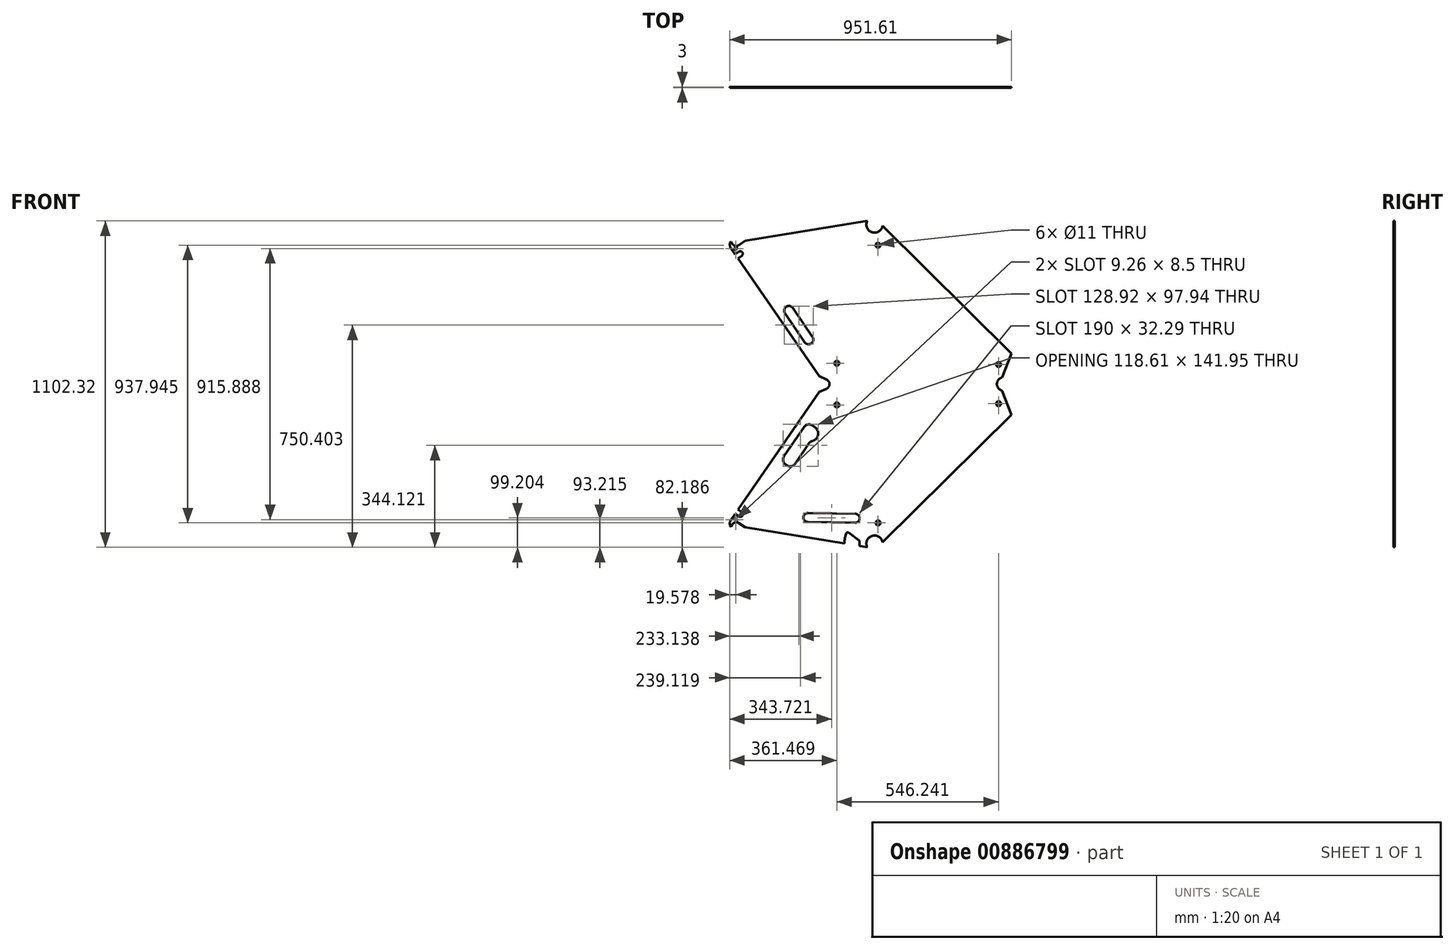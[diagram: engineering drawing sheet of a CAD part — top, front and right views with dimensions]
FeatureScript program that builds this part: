
annotation { "Feature Type Name" : "Feature", "Feature Type Description" : "" }
export const myFeature = defineFeature(function(context is Context, id is Id, definition is map)
    precondition{}
    {
        {
            var Q0;
            Q0=qCreatedBy(makeId("Front.planeOp"),FACE);
            var sketch = newSketch(context, id + "F0", { "sketchPlane" : qUnion([Q0])});
            skCircle(sketch, "E0", {"center": v(1053.9, -134.2) * mm, "radius": 17 * mm, "construction": true});
            skCircle(sketch, "E1", {"center": v(1053.9, -134.2) * mm, "radius": 21.5 * mm, "construction": true});
            skLineSegment(sketch, "E2", {"start": v(622.48, -20.32) * mm, "end": v(871.92, 345.36) * mm, "construction": true});
            skLineSegment(sketch, "E3", {"start": v(615.02, -14.4) * mm, "end": v(879.24, 372.95) * mm, "construction": true});
            skLineSegment(sketch, "E4", {"start": v(1053.9, -134.22) * mm, "end": v(865.03, 414.2) * mm, "construction": true});
            skLineSegment(sketch, "E5", {"start": v(1034.15, -125.7) * mm, "end": v(850, 409.01) * mm, "construction": true});
            skLineSegment(sketch, "E6", {"start": v(861.66, 381.3) * mm, "end": v(851.9, 409.67) * mm, "construction": true});
            skLineSegment(sketch, "E7", {"start": v(1064.21, -115.34) * mm, "end": v(880.07, 419.37) * mm, "construction": true});
            skLineSegment(sketch, "E8", {"start": v(1053.9, -134.2) * mm, "end": v(645.8, -73.78) * mm, "construction": true});
            skLineSegment(sketch, "E9", {"start": v(743.09, -99.4) * mm, "end": v(644.17, -84.76) * mm, "construction": true});
            skLineSegment(sketch, "E10", {"start": v(746.34, -77.44) * mm, "end": v(647.42, -62.8) * mm, "construction": true});
            skLineSegment(sketch, "E11", {"start": v(1035.36, -145.1) * mm, "end": v(841.66, -116.43) * mm, "construction": true});
            skLineSegment(sketch, "E12", {"start": v(1039.32, -118.4) * mm, "end": v(845.61, -89.72) * mm, "construction": true});
            skLineSegment(sketch, "E13", {"start": v(966.15, -134.86) * mm, "end": v(995.58, -139.21) * mm, "construction": true});
            skLineSegment(sketch, "E14", {"start": v(960.23, -139.03) * mm, "end": v(994.85, -144.16) * mm, "construction": true});
            skLineSegment(sketch, "E15", {"start": v(963.6, -143.58) * mm, "end": v(964.04, -140.6) * mm, "construction": true});
            skArc(sketch, "E16", {"start": v(959.64, -143) * mm, "mid": v(959.83, -143.73) * mm, "end": v(960.48, -144.13) * mm, "construction": true});
            skLineSegment(sketch, "E17", {"start": v(960.48, -144.13) * mm, "end": v(962.46, -144.42) * mm, "construction": true});
            skArc(sketch, "E18", {"start": v(962.46, -144.42) * mm, "mid": v(963.2, -144.23) * mm, "end": v(963.6, -143.58) * mm, "construction": true});
            skLineSegment(sketch, "E19", {"start": v(965.3, -133.72) * mm, "end": v(967.21, -120.86) * mm, "construction": true});
            skLineSegment(sketch, "E20", {"start": v(963, -120.24) * mm, "end": v(959.64, -143) * mm, "construction": true});
            skLineSegment(sketch, "E21", {"start": v(962.42, -124.2) * mm, "end": v(966.63, -124.82) * mm, "construction": true});
            skArc(sketch, "E22", {"start": v(965.17, -139.77) * mm, "mid": v(964.43, -139.95) * mm, "end": v(964.04, -140.6) * mm, "construction": true});
            skLineSegment(sketch, "E23", {"start": v(961.7, -129.14) * mm, "end": v(965.9, -129.76) * mm, "construction": true});
            skLineSegment(sketch, "E24", {"start": v(960.08, -126.38) * mm, "end": v(968.24, -127.58) * mm, "construction": true});
            skLineSegment(sketch, "E25", {"start": v(974.82, -141.2) * mm, "end": v(975.55, -136.25) * mm, "construction": true});
            skArc(sketch, "E26", {"start": v(965.3, -133.72) * mm, "mid": v(965.5, -134.46) * mm, "end": v(966.15, -134.86) * mm, "construction": true});
            skLineSegment(sketch, "E27", {"start": v(964.14, -119.4) * mm, "end": v(966.37, -119.73) * mm, "construction": true});
            skArc(sketch, "E28", {"start": v(964.14, -119.4) * mm, "mid": v(963.4, -119.58) * mm, "end": v(963, -120.24) * mm, "construction": true});
            skArc(sketch, "E29", {"start": v(967.21, -120.86) * mm, "mid": v(967.03, -120.12) * mm, "end": v(966.37, -119.73) * mm, "construction": true});
            skLineSegment(sketch, "E30", {"start": v(995.58, -139.21) * mm, "end": v(999.8, -144.9) * mm, "construction": true});
            skLineSegment(sketch, "E31", {"start": v(979.72, -143.94) * mm, "end": v(981.04, -135.04) * mm, "construction": true});
            skArc(sketch, "E32", {"start": v(995.7, -145.3) * mm, "mid": v(995.5, -144.55) * mm, "end": v(994.85, -144.16) * mm, "construction": true});
            skArc(sketch, "E33", {"start": v(995.25, -148.26) * mm, "mid": v(995.44, -149) * mm, "end": v(996.1, -149.4) * mm, "construction": true});
            skArc(sketch, "E34", {"start": v(998.07, -149.7) * mm, "mid": v(998.82, -149.5) * mm, "end": v(999.2, -148.85) * mm, "construction": true});
            skLineSegment(sketch, "E35", {"start": v(996.1, -149.4) * mm, "end": v(998.07, -149.7) * mm, "construction": true});
            skLineSegment(sketch, "E36", {"start": v(999.2, -148.85) * mm, "end": v(999.8, -144.9) * mm, "construction": true});
            skLineSegment(sketch, "E37", {"start": v(995.25, -148.26) * mm, "end": v(995.7, -145.3) * mm, "construction": true});
            skLineSegment(sketch, "E38", {"start": v(985.2, -142.73) * mm, "end": v(985.94, -137.79) * mm, "construction": true});
            skLineSegment(sketch, "E39", {"start": v(995.47, -146.78) * mm, "end": v(993.6, -159.38) * mm, "construction": true});
            skLineSegment(sketch, "E40", {"start": v(850, 409.01) * mm, "end": v(880.07, 419.37) * mm, "construction": true});
            skLineSegment(sketch, "E41", {"start": v(859.77, 380.65) * mm, "end": v(861.66, 381.3) * mm, "construction": true});
            skLineSegment(sketch, "E42", {"start": v(1053.9, -134.22) * mm, "end": v(1520.05, 326.73) * mm, "construction": true});
            skLineSegment(sketch, "E43", {"start": v(1081.03, -129.75) * mm, "end": v(1510.36, 294.78) * mm, "construction": true});
            skLineSegment(sketch, "E44", {"start": v(1060.7, -105.14) * mm, "end": v(1497.91, 327.2) * mm, "construction": true});
            skLineSegment(sketch, "E45", {"start": v(879.24, 372.95) * mm, "end": v(1402.67, 372.95) * mm, "construction": true});
            skLineSegment(sketch, "E46", {"start": v(901.53, 357.05) * mm, "end": v(1486.45, 357.05) * mm, "construction": true});
            skLineSegment(sketch, "E47", {"start": v(890.58, 388.85) * mm, "end": v(1474.25, 388.85) * mm, "construction": true});
            skArc(sketch, "E48", {"start": v(1486.5, 356.93) * mm, "mid": v(1487.54, 375.64) * mm, "end": v(1474.25, 388.85) * mm, "construction": true});
            skArc(sketch, "E49", {"start": v(890.58, 388.85) * mm, "mid": v(888.92, 370.5) * mm, "end": v(901.53, 357.05) * mm, "construction": true});
            skArc(sketch, "E50", {"start": v(1510.36, 294.78) * mm, "mid": v(1511.76, 313.92) * mm, "end": v(1497.91, 327.2) * mm, "construction": true});
            skArc(sketch, "E51", {"start": v(919.09, -223.5) * mm, "mid": v(918.34, -223.31) * mm, "end": v(917.6, -223.13) * mm, "construction": true});
            skFitSpline(sketch, "E52", {"points": [v(871.92, 345.36) * mm, v(875.7, 355.52) * mm, v(881.2, 370.3) * mm, v(868.26, 368.37) * mm, v(864.2, 367.77) * mm], "construction": true});
            skLineSegment(sketch, "E53", {"start": v(587.46, -71.43) * mm, "end": v(605.08, -83.05) * mm, "construction": true});
            skLineSegment(sketch, "E54", {"start": v(584.15, -63.19) * mm, "end": v(613.37, -82.46) * mm, "construction": true});
            skLineSegment(sketch, "E55", {"start": v(607.46, -8.63) * mm, "end": v(607.4, -8.7) * mm, "construction": true});
            skLineSegment(sketch, "E56", {"start": v(644.18, -84.66) * mm, "end": v(644.29, -83.94) * mm, "construction": true});
            skLineSegment(sketch, "E57", {"start": v(644.18, -84.66) * mm, "end": v(622.66, -81.47) * mm, "construction": true});
            skArc(sketch, "E58", {"start": v(644.63, -83.68) * mm, "mid": v(644.4, -83.74) * mm, "end": v(644.29, -83.94) * mm, "construction": true});
            skLineSegment(sketch, "E59", {"start": v(644.18, -84.66) * mm, "end": v(644.19, -84.63) * mm, "construction": true});
            skArc(sketch, "E60", {"start": v(617.78, -52.64) * mm, "mid": v(628.06, -58.54) * mm, "end": v(639.47, -61.73) * mm, "construction": true});
            skLineSegment(sketch, "E61", {"start": v(670.48, -77.43) * mm, "end": v(577.33, -63.64) * mm, "construction": true});
            skLineSegment(sketch, "E62", {"start": v(647.4, -62.9) * mm, "end": v(639.47, -61.73) * mm, "construction": true});
            skArc(sketch, "E63", {"start": v(647.3, -63.56) * mm, "mid": v(647.36, -63.78) * mm, "end": v(647.56, -63.9) * mm, "construction": true});
            skLineSegment(sketch, "E64", {"start": v(647.3, -63.56) * mm, "end": v(647.4, -62.9) * mm, "construction": true});
            skArc(sketch, "E65", {"start": v(614, -32.51) * mm, "mid": v(611.92, -43.32) * mm, "end": v(617.78, -52.64) * mm, "construction": true});
            skLineSegment(sketch, "E66", {"start": v(614, -32.51) * mm, "end": v(622.56, -20.17) * mm, "construction": true});
            skLineSegment(sketch, "E67", {"start": v(576.98, -64.11) * mm, "end": v(629.71, 4.8) * mm, "construction": true});
            skArc(sketch, "E68", {"start": v(572.75, -54.03) * mm, "mid": v(569.56, -71.65) * mm, "end": v(582.02, -84.5) * mm, "construction": true});
            skLineSegment(sketch, "E69", {"start": v(607.46, -8.63) * mm, "end": v(608.42, -9.36) * mm, "construction": true});
            skArc(sketch, "E70", {"start": v(621.55, -19.02) * mm, "mid": v(621.5, -19.24) * mm, "end": v(621.6, -19.44) * mm, "construction": true});
            skLineSegment(sketch, "E71", {"start": v(621.6, -19.44) * mm, "end": v(622.56, -20.17) * mm, "construction": true});
            skArc(sketch, "E72", {"start": v(608.42, -9.36) * mm, "mid": v(608.64, -9.42) * mm, "end": v(608.84, -9.3) * mm, "construction": true});
            skLineSegment(sketch, "E73", {"start": v(608.42, -9.36) * mm, "end": v(607.46, -8.63) * mm, "construction": true});
            skLineSegment(sketch, "E74", {"start": v(619.71, -24.29) * mm, "end": v(604.42, -12.6) * mm, "construction": true});
            skCircle(sketch, "E75", {"center": v(600.85, -74.2) * mm, "radius": 5 * mm, "construction": true});
            skLineSegment(sketch, "E76", {"start": v(621.6, -19.44) * mm, "end": v(608.42, -9.36) * mm, "construction": true});
            skLineSegment(sketch, "E77", {"start": v(841.66, -116.43) * mm, "end": v(743.09, -99.4) * mm, "construction": true});
            skLineSegment(sketch, "E78", {"start": v(746.34, -77.44) * mm, "end": v(845.61, -89.72) * mm, "construction": true});
            skEllipse(sketch, "E79", {"center": v(843.64, -103.07) * mm, "majorRadius": 13.5 * mm, "minorRadius": 8.5 * mm, "majorAxis": v(-0.15, -0.99), "construction": true});
            skCircle(sketch, "E80", {"center": v(795.03, 249.5) * mm, "radius": 9.5 * mm, "construction": true});
            skLineSegment(sketch, "E81", {"start": v(796.02, 244.3) * mm, "end": v(795.95, 244.64) * mm, "construction": true});
            skLineSegment(sketch, "E82", {"start": v(796.02, 244.3) * mm, "end": v(789.82, 248.52) * mm, "construction": true});
            skLineSegment(sketch, "E83", {"start": v(784, 242.2) * mm, "end": v(792.26, 236.56) * mm, "construction": true});
            skLineSegment(sketch, "E84", {"start": v(792.26, 236.56) * mm, "end": v(793.8, 238.84) * mm, "construction": true});
            skLineSegment(sketch, "E85", {"start": v(791.91, 236.5) * mm, "end": v(792.26, 236.56) * mm, "construction": true});
            skLineSegment(sketch, "E86", {"start": v(795.95, 244.64) * mm, "end": v(790.17, 248.58) * mm, "construction": true});
            skLineSegment(sketch, "E87", {"start": v(791.91, 236.5) * mm, "end": v(784.06, 241.85) * mm, "construction": true});
            skLineSegment(sketch, "E88", {"start": v(789.96, 238.43) * mm, "end": v(794.75, 245.46) * mm, "construction": true});
            skLineSegment(sketch, "E89", {"start": v(790.2, 238) * mm, "end": v(795.12, 245.2) * mm, "construction": true});
            skLineSegment(sketch, "E90", {"start": v(793.8, 238.84) * mm, "end": v(785.55, 244.47) * mm, "construction": true});
            skLineSegment(sketch, "E91", {"start": v(792.78, 239.54) * mm, "end": v(796.02, 244.3) * mm, "construction": true});
            skArc(sketch, "E92", {"start": v(962.06, -126.67) * mm, "mid": v(930.44, 82.62) * mm, "end": v(787.99, 239.18) * mm, "construction": true});
            skLineSegment(sketch, "E93", {"start": v(702.12, -93.34) * mm, "end": v(670.46, -88.65) * mm, "construction": true});
            skCircle(sketch, "E94", {"center": v(1053.9, -134.2) * mm, "radius": 94.9 * mm, "construction": true});
            skCircle(sketch, "E95", {"center": v(600.85, -74.2) * mm, "radius": 41.4 * mm, "construction": true});
            skLineSegment(sketch, "E96", {"start": v(1055.81, -39.3) * mm, "end": v(601.44, -32.8) * mm, "construction": true});
            skLineSegment(sketch, "E97", {"start": v(1469.36, 401.56) * mm, "end": v(1507.64, 416.26) * mm, "construction": true});
            skLineSegment(sketch, "E98", {"start": v(1507.64, 416.26) * mm, "end": v(1552.44, 299.56) * mm, "construction": true});
            skLineSegment(sketch, "E99", {"start": v(1552.44, 299.56) * mm, "end": v(1514.16, 284.87) * mm, "construction": true});
            skLineSegment(sketch, "E100", {"start": v(1514.16, 284.87) * mm, "end": v(1469.36, 401.56) * mm, "construction": true});
            skLineSegment(sketch, "E101", {"start": v(1516.78, 301.13) * mm, "end": v(1081.03, -129.75) * mm});
            skLineSegment(sketch, "E102", {"start": v(572.75, -54.03) * mm, "end": v(878.77, 388.85) * mm, "construction": true});
            skArc(sketch, "E103", {"start": v(1081.03, -129.75) * mm, "mid": v(1045.48, -108.05) * mm, "end": v(1029.25, -146.41) * mm});
            skLineSegment(sketch, "E104.trimOffspring", {"start": v(1029.25, -146.41) * mm, "end": v(617.52, -79.2) * mm});
            skCircle(sketch, "E105", {"center": v(926.64, 334.5) * mm, "radius": 4 * mm, "construction": true});
            skCircle(sketch, "E106", {"center": v(1472.88, 338.55) * mm, "radius": 4 * mm, "construction": true});
            skCircle(sketch, "E107", {"center": v(1065.9, -64.22) * mm, "radius": 4 * mm, "construction": true});
            skLineSegment(sketch, "E108", {"start": v(1053.9, -134.22) * mm, "end": v(1237.28, -134.22) * mm, "construction": true});
            skLineSegment(sketch, "E109", {"start": v(1053.9, -134.22) * mm, "end": v(1053.9, 23.55) * mm, "construction": true});
            skCircle(sketch, "E110", {"center": v(866.64, 414.5) * mm, "radius": 25 * mm, "construction": true});
            skCircle(sketch, "E111", {"center": v(1489.1, 401.54) * mm, "radius": 28.6 * mm, "construction": true});
            skLineSegment(sketch, "E112", {"start": v(1516.78, 301.13) * mm, "end": v(1482.36, 388.85) * mm});
            skLineSegment(sketch, "E113.trimOffspring", {"start": v(875.12, 388.85) * mm, "end": v(1482.36, 388.85) * mm});
            skCircle(sketch, "E114", {"center": v(600.85, -74.2) * mm, "radius": 312.5 * mm, "construction": true});
            skLineSegment(sketch, "E115.0", {"start": v(568.9, -54.33) * mm, "end": v(583.1, -33.76) * mm});
            skArc(sketch, "E116", {"start": v(568.9, -54.33) * mm, "mid": v(565.18, -65.8) * mm, "end": v(568.38, -77.42) * mm});
            skLineSegment(sketch, "E117.trimOffspring", {"start": v(601.35, -7.36) * mm, "end": v(875.12, 388.85) * mm});
            skArc(sketch, "E118", {"start": v(594.2, -30.39) * mm, "mid": v(610.2, -27.47) * mm, "end": v(607.28, -11.47) * mm, "construction": true});
            skLineSegment(sketch, "E119", {"start": v(600.85, -74.2) * mm, "end": v(600.85, 11.26) * mm, "construction": true});
            skLineSegment(sketch, "E120", {"start": v(607.28, -11.47) * mm, "end": v(601.35, -7.36) * mm, "construction": true});
            skLineSegment(sketch, "E121", {"start": v(601.35, -7.36) * mm, "end": v(592.77, -19.77) * mm});
            skLineSegment(sketch, "E122", {"start": v(583.1, -33.76) * mm, "end": v(595.7, -42.46) * mm});
            skLineSegment(sketch, "E123", {"start": v(617.52, -79.2) * mm, "end": v(594.98, -64.34) * mm});
            skArc(sketch, "E124", {"start": v(587.46, -59.38) * mm, "mid": v(582.95, -58.52) * mm, "end": v(579.15, -61.1) * mm, "construction": true});
            skLineSegment(sketch, "E125", {"start": v(574.2, -68.6) * mm, "end": v(568.38, -77.42) * mm});
            skLineSegment(sketch, "E126", {"start": v(584.16, -64.4) * mm, "end": v(568.9, -54.33) * mm, "construction": true});
            skArc(sketch, "E127", {"start": v(585.6, -49.56) * mm, "mid": v(580.67, -50.4) * mm, "end": v(581.63, -55.32) * mm});
            skArc(sketch, "E128", {"start": v(595.7, -42.46) * mm, "mid": v(607.52, -40.3) * mm, "end": v(605.36, -28.47) * mm});
            skLineSegment(sketch, "E129", {"start": v(605.36, -28.47) * mm, "end": v(592.77, -19.77) * mm});
            skLineSegment(sketch, "E130", {"start": v(605.36, -28.47) * mm, "end": v(595.7, -42.46) * mm, "construction": true});
            skLineSegment(sketch, "E131", {"start": v(585.48, -49.47) * mm, "end": v(587.95, -51.18) * mm});
            skLineSegment(sketch, "E132", {"start": v(583.55, -52.4) * mm, "end": v(581.63, -55.32) * mm, "construction": true});
            skLineSegment(sketch, "E133", {"start": v(583.55, -52.4) * mm, "end": v(585.48, -49.47) * mm});
            skLineSegment(sketch, "E134", {"start": v(581.63, -55.32) * mm, "end": v(584.13, -56.97) * mm});
            skArc(sketch, "E135", {"start": v(584.13, -56.97) * mm, "mid": v(588.87, -55.94) * mm, "end": v(587.95, -51.18) * mm});
            skPoint(sketch, "E136.newPointB", {"position": v(587.46, -59.38) * mm});
            skArc(sketch, "E136.filletArc", {"start": v(594.98, -64.34) * mm, "mid": v(583.7, -62.17) * mm, "end": v(574.2, -68.6) * mm});
            skSolve(sketch);
        }
        {
            var Q0;
            Q0=qSketchRegion(id+"F0",true);
            extrude(context, id + "F1", {"entities" : qUnion([Q0]), "depth" : 3 * mm, "offsetDistance" : 25 * mm});
        }
        {
            var Q0;
            Q0=makeQuery(id+"F1.opExtrude","SWEPT_FACE",FACE,{"disambiguationData":[OSD([sQuery(id+"F0.wireOp",EDGE,"E113.trimOffspring")])]});
            cPlane(context, id + "F2", {"entities" : qUnion([Q0]), "cplaneType" : CPlaneType.OFFSET, "offset" : 15.9 * mm, "width" : 150 * mm, "height" : 150 * mm});
        }
        {
            var Q0;
            Q0=makeQuery(id+"F1.opExtrude","SWEPT_BODY",BODY,{"disambiguationData":[OSD([sQuery(id+"F0.wireOp",EDGE,"a49be1ca-efc1-4c5e-93b1-82285a78bd7e"),sQuery(id+"F0.wireOp",EDGE,"E53"),sQuery(id+"F0.wireOp",EDGE,"00abc04f-36b8-44c4-b012-511981e3aebb"),sQuery(id+"F0.wireOp",EDGE,"ef0dd70a-e356-403d-8d9f-21a9ec4b274b"),sQuery(id+"F0.wireOp",EDGE,"c0fece56-cd10-4327-9040-2cab23e675d4"),sQuery(id+"F0.wireOp",EDGE,"81bee024-3d0e-4fca-8609-8fb9e83f8aac"),sQuery(id+"F0.wireOp",EDGE,"E68"),sQuery(id+"F0.wireOp",EDGE,"PVY0APLz-6rdr-JrDk-CvCb-vWmYWycaJObT"),sQuery(id+"F0.wireOp",EDGE,"rSiPkJzu-22ck-wLmw-T34Z-YrS7vC3DeLN9"),sQuery(id+"F0.wireOp",EDGE,"E101"),sQuery(id+"F0.wireOp",EDGE,"E102"),sQuery(id+"F0.wireOp",EDGE,"E103"),sQuery(id+"F0.wireOp",EDGE,"E104.trimOffspring")])]});
            var Q1;
            Q1=qCreatedBy(id+"F2.planeOp",FACE);
            mirror(context, id + "F3", {"entities" : qUnion([Q0]), "mirrorPlane" : qUnion([Q1])});
        }
        {
            var Q0;
            Q0=makeQuery(id+"F1.opExtrude","CAP_FACE",FACE,{"disambiguationData":[OSD([sQuery(id+"F0.wireOp",EDGE,"a49be1ca-efc1-4c5e-93b1-82285a78bd7e"),sQuery(id+"F0.wireOp",EDGE,"E53"),sQuery(id+"F0.wireOp",EDGE,"00abc04f-36b8-44c4-b012-511981e3aebb"),sQuery(id+"F0.wireOp",EDGE,"ef0dd70a-e356-403d-8d9f-21a9ec4b274b"),sQuery(id+"F0.wireOp",EDGE,"c0fece56-cd10-4327-9040-2cab23e675d4"),sQuery(id+"F0.wireOp",EDGE,"81bee024-3d0e-4fca-8609-8fb9e83f8aac"),sQuery(id+"F0.wireOp",EDGE,"E68"),sQuery(id+"F0.wireOp",EDGE,"PVY0APLz-6rdr-JrDk-CvCb-vWmYWycaJObT"),sQuery(id+"F0.wireOp",EDGE,"rSiPkJzu-22ck-wLmw-T34Z-YrS7vC3DeLN9"),sQuery(id+"F0.wireOp",EDGE,"E101"),sQuery(id+"F0.wireOp",EDGE,"E102"),sQuery(id+"F0.wireOp",EDGE,"E103"),sQuery(id+"F0.wireOp",EDGE,"E104.trimOffspring")])],"isStart":false});
            var sketch = newSketch(context, id + "F4", { "sketchPlane" : qUnion([Q0])});
            skArc(sketch, "E137", {"start": v(1484.73, 426.68) * mm, "mid": v(1467.24, 404.75) * mm, "end": v(1484.73, 382.81) * mm});
            skArc(sketch, "E138", {"start": v(891.59, 388.85) * mm, "mid": v(901.78, 404.75) * mm, "end": v(891.59, 420.65) * mm});
            skLineSegment(sketch, "E139", {"start": v(884.28, 404.75) * mm, "end": v(1489.74, 404.75) * mm, "construction": true});
            skLineSegment(sketch, "E140", {"start": v(891.59, 420.65) * mm, "end": v(867.46, 431.74) * mm});
            skLineSegment(sketch, "E141", {"start": v(891.59, 388.85) * mm, "end": v(867.46, 377.75) * mm});
            skLineSegment(sketch, "E142.0", {"start": v(1516.78, 508.37) * mm, "end": v(1482.36, 420.65) * mm, "construction": true});
            skLineSegment(sketch, "E143", {"start": v(1482.36, 388.85) * mm, "end": v(1516.78, 301.13) * mm, "construction": true});
            skLineSegment(sketch, "E144", {"start": v(891.59, 420.65) * mm, "end": v(1473.82, 420.65) * mm});
            skLineSegment(sketch, "E145", {"start": v(891.59, 388.85) * mm, "end": v(1473.82, 388.85) * mm});
            skSolve(sketch);
        }
        {
            var Q0;
            Q0=qSketchRegion(id+"F4",true);
            var Q1;
            Q1=makeQuery(id+"F3.opPattern","COPY",FACE,{"derivedFrom":makeQuery(id+"F1.opExtrude","CAP_FACE",FACE,{"disambiguationData":[OSD([sQuery(id+"F0.wireOp",EDGE,"a49be1ca-efc1-4c5e-93b1-82285a78bd7e"),sQuery(id+"F0.wireOp",EDGE,"E53"),sQuery(id+"F0.wireOp",EDGE,"00abc04f-36b8-44c4-b012-511981e3aebb"),sQuery(id+"F0.wireOp",EDGE,"ef0dd70a-e356-403d-8d9f-21a9ec4b274b"),sQuery(id+"F0.wireOp",EDGE,"c0fece56-cd10-4327-9040-2cab23e675d4"),sQuery(id+"F0.wireOp",EDGE,"81bee024-3d0e-4fca-8609-8fb9e83f8aac"),sQuery(id+"F0.wireOp",EDGE,"E68"),sQuery(id+"F0.wireOp",EDGE,"PVY0APLz-6rdr-JrDk-CvCb-vWmYWycaJObT"),sQuery(id+"F0.wireOp",EDGE,"rSiPkJzu-22ck-wLmw-T34Z-YrS7vC3DeLN9"),sQuery(id+"F0.wireOp",EDGE,"E101"),sQuery(id+"F0.wireOp",EDGE,"E102"),sQuery(id+"F0.wireOp",EDGE,"E103"),sQuery(id+"F0.wireOp",EDGE,"E104.trimOffspring")])],"isStart":true}),"instanceName":"1"});
            extrude(context, id + "F5", {"entities" : qUnion([Q0]), "operationType" : NewBodyOperationType.ADD, "endBound" : BoundingType.UP_TO_SURFACE, "oppositeDirection" : true, "depth" : 65 * mm, "endBoundEntityFace" : qUnion([Q1]), "offsetDistance" : 25 * mm});
        }
        {
            var Q0;
            {var subQ0=makeQuery(id+"F1.opExtrude","CAP_FACE",FACE,{"disambiguationData":[OSD([sQuery(id+"F0.wireOp",EDGE,"a49be1ca-efc1-4c5e-93b1-82285a78bd7e"),sQuery(id+"F0.wireOp",EDGE,"E53"),sQuery(id+"F0.wireOp",EDGE,"00abc04f-36b8-44c4-b012-511981e3aebb"),sQuery(id+"F0.wireOp",EDGE,"ef0dd70a-e356-403d-8d9f-21a9ec4b274b"),sQuery(id+"F0.wireOp",EDGE,"81bee024-3d0e-4fca-8609-8fb9e83f8aac"),sQuery(id+"F0.wireOp",EDGE,"E68"),sQuery(id+"F0.wireOp",EDGE,"E101"),sQuery(id+"F0.wireOp",EDGE,"E102"),sQuery(id+"F0.wireOp",EDGE,"E103"),sQuery(id+"F0.wireOp",EDGE,"E104.trimOffspring"),sQuery(id+"F0.wireOp",EDGE,"E105"),sQuery(id+"F0.wireOp",EDGE,"E106"),sQuery(id+"F0.wireOp",EDGE,"E107"),sQuery(id+"F0.wireOp",EDGE,"E112"),sQuery(id+"F0.wireOp",EDGE,"E113.trimOffspring")])],"isStart":false});Q0=makeQuery(id+"F5.boolean.opBoolean","MERGE",FACE,{"derivedFrom":[subQ0,makeQuery(id+"F3.opPattern","COPY",FACE,{"derivedFrom":subQ0,"instanceName":"1"}),makeQuery(id+"F5.opExtrude","CAP_FACE",FACE,{"disambiguationData":[OSD([sQuery(id+"F4.wireOp",EDGE,"E137"),sQuery(id+"F4.wireOp",EDGE,"E138"),sQuery(id+"F4.wireOp",EDGE,"E144"),sQuery(id+"F4.wireOp",EDGE,"E145")])],"isStart":true})]});}
            var sketch = newSketch(context, id + "F6", { "sketchPlane" : qUnion([Q0])});
            skLineSegment(sketch, "E146.0", {"start": v(891.59, 420.65) * mm, "end": v(867.46, 431.74) * mm});
            skLineSegment(sketch, "E146.1", {"start": v(891.59, 388.85) * mm, "end": v(867.46, 377.75) * mm});
            skArc(sketch, "E147.0", {"start": v(891.59, 388.85) * mm, "mid": v(901.78, 404.75) * mm, "end": v(891.59, 420.65) * mm});
            skLineSegment(sketch, "E148", {"start": v(867.46, 431.74) * mm, "end": v(867.46, 377.75) * mm});
            skArc(sketch, "E149.0", {"start": v(1484.73, 426.68) * mm, "mid": v(1467.24, 404.75) * mm, "end": v(1484.73, 382.81) * mm});
            skLineSegment(sketch, "E150", {"start": v(1484.73, 426.68) * mm, "end": v(1484.73, 382.81) * mm});
            skSolve(sketch);
        }
        {
            var Q0;
            Q0=qSketchRegion(id+"F6",true);
            extrude(context, id + "F7", {"entities" : qUnion([Q0]), "operationType" : NewBodyOperationType.REMOVE, "oppositeDirection" : true, "depth" : 25 * mm, "offsetDistance" : 25 * mm});
        }
        {
            var Q0;
            {var subQ0=makeQuery(id+"F1.opExtrude","CAP_FACE",FACE,{"disambiguationData":[OSD([sQuery(id+"F0.wireOp",EDGE,"a49be1ca-efc1-4c5e-93b1-82285a78bd7e"),sQuery(id+"F0.wireOp",EDGE,"E53"),sQuery(id+"F0.wireOp",EDGE,"00abc04f-36b8-44c4-b012-511981e3aebb"),sQuery(id+"F0.wireOp",EDGE,"ef0dd70a-e356-403d-8d9f-21a9ec4b274b"),sQuery(id+"F0.wireOp",EDGE,"81bee024-3d0e-4fca-8609-8fb9e83f8aac"),sQuery(id+"F0.wireOp",EDGE,"E68"),sQuery(id+"F0.wireOp",EDGE,"PVY0APLz-6rdr-JrDk-CvCb-vWmYWycaJObT"),sQuery(id+"F0.wireOp",EDGE,"rSiPkJzu-22ck-wLmw-T34Z-YrS7vC3DeLN9"),sQuery(id+"F0.wireOp",EDGE,"E101"),sQuery(id+"F0.wireOp",EDGE,"E102"),sQuery(id+"F0.wireOp",EDGE,"E103"),sQuery(id+"F0.wireOp",EDGE,"E104.trimOffspring"),sQuery(id+"F0.wireOp",EDGE,"E105"),sQuery(id+"F0.wireOp",EDGE,"E106"),sQuery(id+"F0.wireOp",EDGE,"E107")])],"isStart":false});Q0=makeQuery(id+"F5.boolean.opBoolean","MERGE",FACE,{"derivedFrom":[subQ0,makeQuery(id+"F3.opPattern","COPY",FACE,{"derivedFrom":subQ0,"instanceName":"1"}),makeQuery(id+"F5.opExtrude","CAP_FACE",FACE,{"disambiguationData":[OSD([sQuery(id+"F4.wireOp",EDGE,"yLFeXnhX-FHJ1-lWFD-LUYU-IVhkZNTNpous"),sQuery(id+"F4.wireOp",EDGE,"25Roz2r3-I6Ic-58va-7k2N-V37a2FIcnueW"),sQuery(id+"F4.wireOp",EDGE,"Mdtmx1y3-Aq5y-VBCD-G2xE-9g1DUSUnupkp"),sQuery(id+"F4.wireOp",EDGE,"31XSQ7MP-bYWI-LpWw-hrBR-gacfVsKKRKhD")])],"isStart":true})]});}
            var sketch = newSketch(context, id + "F8", { "sketchPlane" : qUnion([Q0])});
            skLineSegment(sketch, "E151.bottom", {"start": v(829.1, -31.06) * mm, "end": v(989.1, -33.35) * mm});
            skLineSegment(sketch, "E151.top", {"start": v(828.68, -61.06) * mm, "end": v(988.68, -63.35) * mm});
            skArc(sketch, "E152", {"start": v(829.1, -31.06) * mm, "mid": v(813.9, -45.85) * mm, "end": v(828.68, -61.06) * mm});
            skArc(sketch, "E153", {"start": v(988.68, -63.35) * mm, "mid": v(1003.89, -48.57) * mm, "end": v(989.1, -33.35) * mm});
            skCircle(sketch, "E154", {"center": v(1053.9, -134.22) * mm, "radius": 101.64 * mm, "construction": true});
            skPoint(sketch, "E155.0", {"position": v(1035.36, -145.1) * mm});
            skLineSegment(sketch, "E156.0", {"start": v(1035.36, -145.1) * mm, "end": v(841.66, -116.43) * mm, "construction": true});
            skPoint(sketch, "E157", {"position": v(952.27, -132.8) * mm});
            skCircle(sketch, "E158", {"center": v(1053.9, -134.22) * mm, "radius": 79.64 * mm, "construction": true});
            skPoint(sketch, "E159", {"position": v(1003.7, -140.42) * mm});
            skCircle(sketch, "E160", {"center": v(1053.9, -134.22) * mm, "radius": 50.57 * mm, "construction": true});
            skCircle(sketch, "E161", {"center": v(1053.9, -134.22) * mm, "radius": 60.57 * mm, "construction": true});
            skArc(sketch, "E162", {"start": v(958.41, -99.39) * mm, "mid": v(953.84, -116.35) * mm, "end": v(952.26, -133.85) * mm});
            skArc(sketch, "E163", {"start": v(966.1, -97.09) * mm, "mid": v(961.67, -96.31) * mm, "end": v(958.41, -99.39) * mm});
            skLineSegment(sketch, "E164", {"start": v(966.1, -97.09) * mm, "end": v(1002.65, -124.23) * mm});
            skArc(sketch, "E165", {"start": v(1003.83, -127.07) * mm, "mid": v(1003.33, -134.68) * mm, "end": v(1003.97, -142.29) * mm});
            skPoint(sketch, "E166.visualSharp", {"position": v(994.9, -120.54) * mm});
            skPoint(sketch, "E167.visualSharp", {"position": v(1003.83, -127.07) * mm});
            skArc(sketch, "E167.filletArc", {"start": v(1003.83, -127.07) * mm, "mid": v(1003.63, -125.49) * mm, "end": v(1002.65, -124.23) * mm});
            skLineSegment(sketch, "E168", {"start": v(1003.97, -142.29) * mm, "end": v(952.26, -133.85) * mm});
            skSolve(sketch);
        }
        {
            var Q0;
            Q0=qSketchRegion(id+"F8",true);
            extrude(context, id + "F9", {"entities" : qUnion([Q0]), "operationType" : NewBodyOperationType.REMOVE, "oppositeDirection" : true, "depth" : 25 * mm, "offsetDistance" : 25 * mm});
        }
        {
            var Q0;
            {var subQ6=sQuery(id+"F4.wireOp",EDGE,"E141");Q0=makeQuery(id+"F4.imprint","IMPRINT",FACE,{"disambiguationData":[TD([[makeQuery(id+"F4.imprint","IMPRINT",EDGE,{"derivedFrom":subQ6}),1.0]])]});}
            var sketch = newSketch(context, id + "F10", { "sketchPlane" : qUnion([Q0])});
            skLineSegment(sketch, "E169", {"start": v(748.46, 160.82) * mm, "end": v(816.08, 259.96) * mm});
            skLineSegment(sketch, "E170", {"start": v(843.88, 265.2) * mm, "end": v(852.14, 259.57) * mm});
            skLineSegment(sketch, "E171", {"start": v(757.84, 130.21) * mm, "end": v(753.71, 133.03) * mm});
            skCircle(sketch, "E172.0", {"center": v(600.85, -74.2) * mm, "radius": 312.5 * mm, "construction": true});
            skLineSegment(sketch, "E172.1", {"start": v(622.48, -20.32) * mm, "end": v(871.92, 345.36) * mm, "construction": true});
            skLineSegment(sketch, "E173.0", {"start": v(884.28, 404.75) * mm, "end": v(1489.74, 404.75) * mm, "construction": true});
            skCircle(sketch, "E174.MirrorC", {"center": v(600.85, 883.7) * mm, "radius": 312.5 * mm, "construction": true});
            skLineSegment(sketch, "E175.MirrorCS", {"start": v(622.48, 829.82) * mm, "end": v(871.92, 464.13) * mm, "construction": true});
            skLineSegment(sketch, "E176", {"start": v(818.34, 546.24) * mm, "end": v(751.84, 643.72) * mm});
            skLineSegment(sketch, "E177", {"start": v(756.04, 665.95) * mm, "end": v(756.04, 665.95) * mm});
            skLineSegment(sketch, "E178", {"start": v(778.28, 661.75) * mm, "end": v(844.77, 564.27) * mm});
            skLineSegment(sketch, "E179", {"start": v(840.57, 542.04) * mm, "end": v(840.57, 542.04) * mm});
            skLineSegment(sketch, "E180.0", {"start": v(797.53, 236.3) * mm, "end": v(785.55, 244.47) * mm, "construction": true});
            skLineSegment(sketch, "E181.MirrorCS", {"start": v(797.53, 573.2) * mm, "end": v(785.55, 565.03) * mm, "construction": true});
            skLineSegment(sketch, "E182", {"start": v(797.53, 573.2) * mm, "end": v(768.19, 553.19) * mm, "construction": true});
            skPoint(sketch, "E183.orphan", {"position": v(793.8, 570.66) * mm});
            skPoint(sketch, "E184.orphan", {"position": v(793.8, 238.84) * mm});
            skLineSegment(sketch, "E185", {"start": v(797.53, 236.3) * mm, "end": v(778.55, 249.24) * mm, "construction": true});
            skPoint(sketch, "E186.visualSharp", {"position": v(827.35, 276.48) * mm});
            skArc(sketch, "E186.filletArc", {"start": v(843.88, 265.2) * mm, "mid": v(828.9, 268.34) * mm, "end": v(816.08, 259.96) * mm});
            skPoint(sketch, "E187.visualSharp", {"position": v(872.79, 245.49) * mm});
            skArc(sketch, "E187.filletArc", {"start": v(842.48, 211.69) * mm, "mid": v(863.19, 232.43) * mm, "end": v(852.14, 259.57) * mm});
            skPoint(sketch, "E188.visualSharp", {"position": v(737.2, 144.3) * mm});
            skArc(sketch, "E188.filletArc", {"start": v(748.46, 160.82) * mm, "mid": v(745.33, 145.84) * mm, "end": v(753.71, 133.03) * mm});
            skPoint(sketch, "E189.visualSharp", {"position": v(782.63, 113.3) * mm});
            skArc(sketch, "E189.filletArc", {"start": v(757.84, 130.21) * mm, "mid": v(772.83, 127.08) * mm, "end": v(785.64, 135.47) * mm});
            skPoint(sketch, "E190.visualSharp", {"position": v(742.83, 656.94) * mm});
            skArc(sketch, "E190.filletArc", {"start": v(756.04, 665.95) * mm, "mid": v(749.34, 655.7) * mm, "end": v(751.84, 643.72) * mm});
            skPoint(sketch, "E191.visualSharp", {"position": v(769.26, 674.97) * mm});
            skArc(sketch, "E191.filletArc", {"start": v(778.28, 661.75) * mm, "mid": v(768.03, 668.46) * mm, "end": v(756.04, 665.95) * mm});
            skPoint(sketch, "E192.visualSharp", {"position": v(853.79, 551.05) * mm});
            skArc(sketch, "E192.filletArc", {"start": v(840.57, 542.04) * mm, "mid": v(847.28, 552.28) * mm, "end": v(844.77, 564.27) * mm});
            skPoint(sketch, "E193.visualSharp", {"position": v(827.35, 533.02) * mm});
            skArc(sketch, "E193.filletArc", {"start": v(818.34, 546.24) * mm, "mid": v(828.58, 539.53) * mm, "end": v(840.57, 542.04) * mm});
            skLineSegment(sketch, "E194", {"start": v(785.64, 135.47) * mm, "end": v(833.6, 205.8) * mm});
            skArc(sketch, "E195", {"start": v(842.48, 211.69) * mm, "mid": v(837.47, 209.6) * mm, "end": v(833.6, 205.8) * mm});
            skSolve(sketch);
        }
        {
            var Q0;
            Q0=qSketchRegion(id+"F10",true);
            extrude(context, id + "F11", {"entities" : qUnion([Q0]), "operationType" : NewBodyOperationType.REMOVE, "endBound" : BoundingType.THROUGH_ALL, "oppositeDirection" : true, "depth" : 25 * mm, "offsetDistance" : 25 * mm});
        }
        {
            var Q0;
            {var subQ7=sQuery(id+"F4.wireOp",EDGE,"E141");Q0=makeQuery(id+"F4.imprint","IMPRINT",FACE,{"disambiguationData":[TD([[makeQuery(id+"F4.imprint","IMPRINT",EDGE,{"derivedFrom":subQ7}),1.0]])]});}
            var Q1;
            {var subQ7=sQuery(id+"F4.wireOp",EDGE,"E141");Q1=makeQuery(id+"F4.imprint","IMPRINT",FACE,{"disambiguationData":[TD([[makeQuery(id+"F4.imprint","IMPRINT",EDGE,{"derivedFrom":subQ7}),1.0]])]});}
            var sketch = newSketch(context, id + "F12", { "sketchPlane" : qUnion([Q0, Q1])});
            skPoint(sketch, "E196.0", {"position": v(926.64, 334.5) * mm});
            skPoint(sketch, "E196.1", {"position": v(1472.88, 338.55) * mm});
            skPoint(sketch, "E196.2", {"position": v(1065.9, -64.22) * mm});
            skPoint(sketch, "E197.MirrorP", {"position": v(926.64, 475) * mm});
            skPoint(sketch, "E198.MirrorP", {"position": v(1472.88, 470.95) * mm});
            skPoint(sketch, "E199.MirrorP", {"position": v(1065.9, 873.72) * mm});
            skSolve(sketch);
        }
        {
            var Q0;
            Q0=sQuery(id+"F12.wireOp",VERTEX,"E199.MirrorP");
            var Q1;
            Q1=sQuery(id+"F12.wireOp",VERTEX,"E197.MirrorP");
            var Q2;
            Q2=sQuery(id+"F12.wireOp",VERTEX,"E198.MirrorP");
            var Q3;
            Q3=sQuery(id+"F0.wireOp",VERTEX,"E105.center");
            var Q4;
            Q4=sQuery(id+"F0.wireOp",VERTEX,"E106.center");
            var Q5;
            Q5=sQuery(id+"F0.wireOp",VERTEX,"E107.center");
            var Q6;
            Q6=sQuery(id+"F12.wireOp",VERTEX,"E196.2");
            var Q7;
            Q7=sQuery(id+"F12.wireOp",VERTEX,"E196.0");
            var Q8;
            Q8=sQuery(id+"F12.wireOp",VERTEX,"E196.1");
            var Q9;
            Q9=makeQuery(id+"F1.opExtrude","SWEPT_BODY",BODY,{"disambiguationData":[OSD([sQuery(id+"F0.wireOp",EDGE,"a49be1ca-efc1-4c5e-93b1-82285a78bd7e"),sQuery(id+"F0.wireOp",EDGE,"E53"),sQuery(id+"F0.wireOp",EDGE,"00abc04f-36b8-44c4-b012-511981e3aebb"),sQuery(id+"F0.wireOp",EDGE,"ef0dd70a-e356-403d-8d9f-21a9ec4b274b"),sQuery(id+"F0.wireOp",EDGE,"81bee024-3d0e-4fca-8609-8fb9e83f8aac"),sQuery(id+"F0.wireOp",EDGE,"E101"),sQuery(id+"F0.wireOp",EDGE,"E103"),sQuery(id+"F0.wireOp",EDGE,"E104.trimOffspring"),sQuery(id+"F0.wireOp",EDGE,"E112"),sQuery(id+"F0.wireOp",EDGE,"E113.trimOffspring"),sQuery(id+"F0.wireOp",EDGE,"E115.0"),sQuery(id+"F0.wireOp",EDGE,"E116"),sQuery(id+"F0.wireOp",EDGE,"E117.trimOffspring"),sQuery(id+"F0.wireOp",EDGE,"E118"),sQuery(id+"F0.wireOp",EDGE,"P7GfUhAO-jVLJ-pUWz-LAII-abDS3YpSmHxf"),sQuery(id+"F0.wireOp",EDGE,"E120")])]});
            hole(context, id + "F13", {"style" : HoleStyle.C_SINK, "endStyle" : HoleEndStyle.THROUGH, "holeDiameter" : 11 * mm, "cSinkDiameter" : 16 * mm, "cSinkAngle" : 90 * degree, "majorDiameter" : 5 * mm, "isTappedThrough" : true, "tappedDepth" : 12 * mm, "tapClearance" : 3, "locations" : qUnion([Q0, Q1, Q2, Q3, Q4, Q5, Q6, Q7, Q8]), "scope" : qUnion([Q9])});
        }
    });
